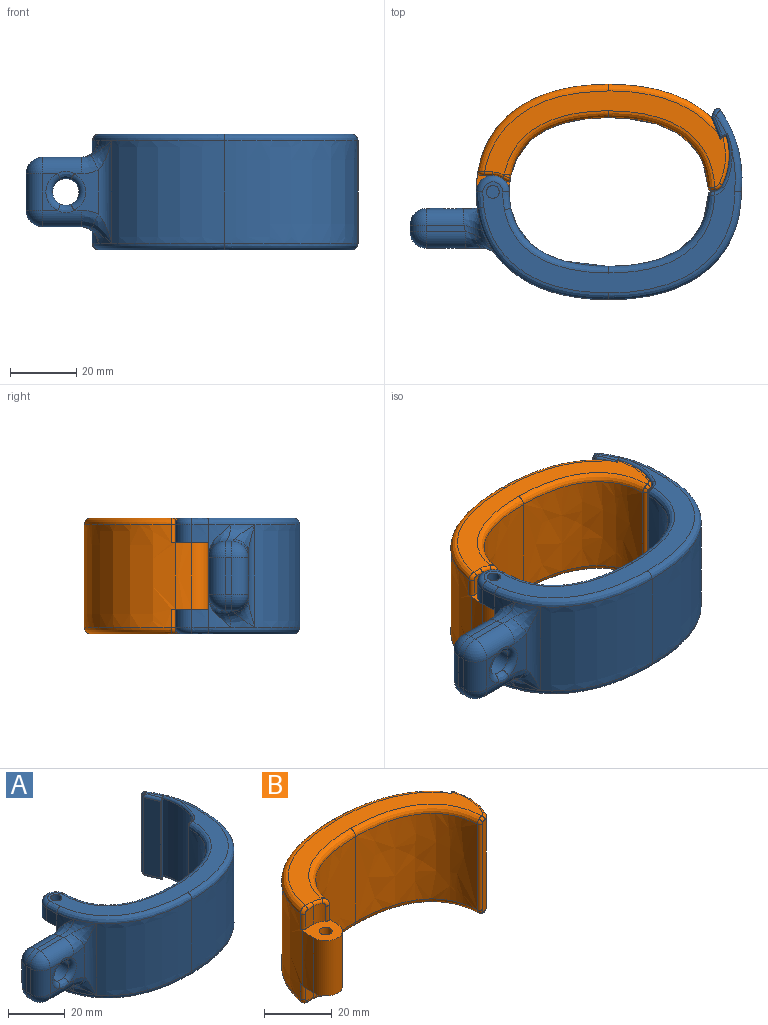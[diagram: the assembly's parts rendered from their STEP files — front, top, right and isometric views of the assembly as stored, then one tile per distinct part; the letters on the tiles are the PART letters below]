
ASSEMBLY  parts=2 mates=1
PART A: 105 faces, bbox 103.2x59x35.3 mm
  f0: cylinder r=1.95mm len=5.5mm, axis (0,0,-1), area 67.4mm2, adj f28,f97
  f1: plane 6.24x3.35mm, normal (0,0,-1), area 6.3mm2, adj f69,f72,f73,f99
  f2: plane 6.24x3.35mm, normal (0,0,1), area 6.3mm2, adj f61,f76,f78,f103
  f3: plane 20x10.6mm, normal (0,1,0), area 132.4mm2, adj f5,f7,f27,f28,f29,f38,f40,f43
  f4: plane 13.52x7.52mm, normal (0,-1,0), area 58.4mm2, adj f36,f41,f44,f54,f55,f81
  f5: extruded ~9.18x6.72mm, area 32mm2, adj f3,f9,f38,f70
  f6: extruded ~34.09x31mm, area 1178.9mm2, adj f13,f36,f62,f70
  f7: extruded ~9.18x6.72mm, area 32mm2, adj f3,f12,f43,f62
  f8: cylinder r=5mm len=10mm, axis (0,0,-1), area 86.4mm2, adj f9,f10,f28,f67
  f9: extruded ~5.5x5mm, area 27.6mm2, adj f5,f8,f28,f68
  f10: extruded ~31x5mm, area 118.7mm2, adj f8,f11,f22,f28,f29,f58,f66,f87
  f11: cylinder r=5mm len=10mm, axis (0,0,-1), area 86.4mm2, adj f10,f12,f29,f59
  f12: extruded ~5.5x5mm, area 27.6mm2, adj f7,f11,f29,f60
  f13: extruded ~40x32.5mm, area 1806.6mm2, adj f6,f14,f63,f71
  f14: cylinder r=36mm len=31mm, axis (0,0,-1), area 809.5mm2, adj f13,f61,f69,f75
  f15: extruded ~33x2.05mm, area 73.3mm2, adj f16,f73,f74,f75,f77,f78
  f16: plane 33x6.17mm, normal (-0.93,-0.37,0), area 219.4mm2, adj f15,f72,f76,f101
  f17: plane 34.65x1.88mm, normal (0.54,-0.84,0), area 60.8mm2, adj f18,f88,f96,f98,f99,f100,f101,f102
  f18: cylinder r=20mm len=33mm, axis (0,0,-1), area 529.8mm2, adj f17,f19,f88,f96
  f19: cylinder r=3mm len=33mm, axis (0,0,-1), area 107.5mm2, adj f18,f20,f89,f90,f94,f95
  f20: plane 32.43x0.3mm, normal (0,1,0), area 9.6mm2, adj f19,f91,f92,f93
  f21: extruded ~31x29.98mm, area 1289.7mm2, adj f22,f56,f64,f92
  f22: extruded ~31x29.55mm, area 1163.8mm2, adj f10,f21,f57,f65
  f23: cylinder r=1.95mm len=7.5mm, axis (0,0,-1), area 91.9mm2, adj f24,f29
  f24: plane 76.22x42.84mm, normal (0,0,1), area 626.1mm2, adj f23,f56,f57,f58,f59,f60,f61,f62
  f25: plane 76.22x42.84mm, normal (0,0,-1), area 638mm2, adj f64,f65,f66,f67,f68,f69,f70,f71
  f26: plane 11x4.6mm, normal (0,1,0), area 22.1mm2, adj f40,f46,f47,f85
  f27: cylinder r=5mm len=20mm, axis (0,0,1), area 131.1mm2, adj f3,f28,f29,f87
  f28: plane 10.08x10.03mm, normal (0,0,1), area 71.5mm2, adj f0,f3,f8,f9,f10,f27,f87
  f29: plane 10.08x10.03mm, normal (0,0,-1), area 71.5mm2, adj f3,f10,f11,f12,f23,f27,f87
  f30: plane 11.78x2mm, normal (0,0,1), area 23mm2, adj f35,f47,f51,f55
  f31: plane 11x4.6mm, normal (0,-1,0), area 22.1mm2, adj f44,f50,f55,f80
  f32: plane 11.78x2mm, normal (0,0,-1), area 23mm2, adj f37,f40,f44,f45
  f33: plane 11x2mm, normal (-1,0,0), area 22mm2, adj f45,f46,f50,f51
  f34: cylinder r=4mm len=8mm, axis (0,1,0), area 201.1mm2, adj f79,f80,f81,f82,f83,f84,f85,f86
  f35: bspline ~16.06x11.16mm, area 34.4mm2, adj f30,f43,f52,f54,f62
  f36: cylinder r=5mm len=31mm, axis (0,0,-1), area 103mm2, adj f4,f6,f39,f52
  f37: bspline ~16.06x11.16mm, area 34.4mm2, adj f32,f38,f39,f41,f70
  f38: bspline ~12.05x11.84mm, area 54.9mm2, adj f3,f5,f37,f40
  f39: bspline ~9.43x7.13mm, area 19.5mm2, adj f36,f37,f41
  f40: cylinder r=5mm len=11.21mm, axis (1,0,0), area 85.3mm2, adj f3,f26,f32,f38,f42,f86
  f41: bspline ~6.48x5.93mm, area 28.7mm2, adj f4,f37,f39,f44
  f42: sphere r=5mm, area 53.5mm2, adj f40,f45,f46
  f43: bspline ~12.05x11.84mm, area 54.9mm2, adj f3,f7,f35,f47
  f44: cylinder r=5mm len=11.78mm, axis (-1,0,0), area 89.8mm2, adj f4,f31,f32,f41,f48,f79
  f45: cylinder r=5mm len=5mm, axis (0,-1,0), area 15.7mm2, adj f32,f33,f42,f48
  f46: cylinder r=5mm len=11mm, axis (0,0,-1), area 86.4mm2, adj f26,f33,f42,f49
  f47: cylinder r=5mm len=11.21mm, axis (-1,0,0), area 85.3mm2, adj f3,f26,f30,f43,f49,f83
  f48: sphere r=5mm, area 39.3mm2, adj f44,f45,f50
  f49: sphere r=5mm, area 53.5mm2, adj f46,f47,f51
  f50: cylinder r=5mm len=11mm, axis (0,0,1), area 86.4mm2, adj f31,f33,f48,f53
  f51: cylinder r=5mm len=5mm, axis (0,1,0), area 15.7mm2, adj f30,f33,f49,f53
  f52: bspline ~9.43x7.13mm, area 19.5mm2, adj f35,f36,f54
  f53: sphere r=5mm, area 39.3mm2, adj f50,f51,f55
  f54: bspline ~7.39x5.93mm, area 28.7mm2, adj f4,f35,f52,f55
  f55: cylinder r=5mm len=11.78mm, axis (1,0,0), area 89.8mm2, adj f4,f30,f31,f53,f54,f82
  f56: bspline ~45.49x24.18mm, area 134.3mm2, adj f21,f24,f57,f93,f94
  f57: bspline ~40.59x27mm, area 121.1mm2, adj f22,f24,f56,f58
  f58: bspline ~6.58x2.5mm, area 16.2mm2, adj f10,f24,f57,f59
  f59: torus R=3mm, axis (0,0,1), area 42.2mm2, adj f11,f24,f58,f60
  f60: bspline ~6.12x2.43mm, area 15.4mm2, adj f12,f24,f59,f62
  f61: torus R=34mm, axis (0,0,1), area 78.4mm2, adj f2,f14,f24,f63,f77,f96,f104
  f62: bspline ~50.61x44.89mm, area 164mm2, adj f6,f7,f24,f35,f60,f63
  f63: bspline ~57.27x33.99mm, area 179.7mm2, adj f13,f24,f61,f62
  f64: bspline ~45.49x24.18mm, area 134.3mm2, adj f21,f25,f65,f90,f91
  f65: bspline ~40.59x27mm, area 121.1mm2, adj f22,f25,f64,f66
  f66: bspline ~7.29x2.64mm, area 16.2mm2, adj f10,f25,f65,f67
  f67: torus R=3mm, axis (0,0,1), area 42.2mm2, adj f8,f25,f66,f68
  f68: bspline ~6.12x2.43mm, area 15.4mm2, adj f9,f25,f67,f70
  f69: torus R=34mm, axis (0,0,1), area 78.4mm2, adj f1,f14,f25,f71,f74,f88,f98
  f70: bspline ~50.61x44.89mm, area 164.1mm2, adj f5,f6,f25,f37,f68,f71
  f71: bspline ~57.27x33.99mm, area 179.7mm2, adj f13,f25,f69,f70
  f72: cylinder r=1mm len=6.54mm, axis (0.37,-0.93,0), area 10mm2, adj f1,f16,f73,f100
  f73: bspline ~2.29x1.78mm, area 1.4mm2, adj f1,f15,f72,f74
  f74: bspline ~3.64x2.42mm, area 5.4mm2, adj f15,f69,f73,f75
  f75: cylinder r=1mm len=31mm, axis (0,0,-1), area 66.5mm2, adj f14,f15,f74,f77
  f76: cylinder r=1mm len=6.54mm, axis (-0.37,0.93,0), area 10mm2, adj f2,f16,f78,f102
  f77: bspline ~3.64x2.42mm, area 5.4mm2, adj f15,f61,f75,f78
  f78: bspline ~2.29x1.78mm, area 1.4mm2, adj f2,f15,f76,f77
  f79: bspline ~6.58x3.08mm, area 13.3mm2, adj f34,f44,f80,f81
  f80: torus R=6mm, axis (0,-1,0), area 34.4mm2, adj f31,f34,f79,f82
  f81: torus R=6mm, axis (0,-1,0), area 34.4mm2, adj f4,f34,f79,f82
  f82: bspline ~6.58x3.08mm, area 13.3mm2, adj f34,f55,f80,f81
  f83: bspline ~6.58x3.08mm, area 13.3mm2, adj f34,f47,f84,f85
  f84: torus R=6mm, axis (0,-1,0), area 34.4mm2, adj f3,f34,f83,f86
  f85: torus R=6mm, axis (0,-1,0), area 34.4mm2, adj f26,f34,f83,f86
  f86: bspline ~6.58x3.08mm, area 13.3mm2, adj f34,f40,f84,f85
  f87: cylinder r=1mm len=20mm, axis (0,0,-1), area 12.5mm2, adj f10,f27,f28,f29
  f88: torus R=21mm, axis (0,0,1), area 25.1mm2, adj f17,f18,f25,f69,f89,f98
  f89: torus R=4mm, axis (0,0,1), area 4.8mm2, adj f19,f25,f88,f90
  f90: bspline ~2.14x1.48mm, area 1.8mm2, adj f19,f64,f89,f91
  f91: bspline ~2.15x1.48mm, area 2mm2, adj f20,f64,f90,f92
  f92: cylinder r=1mm len=31mm, axis (0,0,-1), area 47.7mm2, adj f20,f21,f91,f93
  f93: bspline ~2.15x1.48mm, area 2mm2, adj f20,f56,f92,f94
  f94: bspline ~2.14x1.48mm, area 1.8mm2, adj f19,f56,f93,f95
  f95: torus R=4mm, axis (0,0,1), area 4.8mm2, adj f19,f24,f94,f96
  f96: torus R=21mm, axis (0,0,1), area 25.1mm2, adj f17,f18,f24,f61,f95,f104
  f97: plane 3.9x3.9mm, normal (0,0,1), area 11.9mm2, adj f0
  f98: bspline ~0.92x0.68mm, area 0.1mm2, adj f17,f69,f88,f99
  f99: cylinder r=0.2mm len=1.2mm, axis (0.84,0.54,0), area 0.4mm2, adj f1,f17,f98,f100
  f100: bspline ~1.13x1mm, area 0.5mm2, adj f17,f72,f99,f101
  f101: cylinder r=0.2mm len=33mm, axis (0,0,-1), area 11.6mm2, adj f16,f17,f100,f102
  f102: bspline ~1.13x1.05mm, area 0.5mm2, adj f17,f76,f101,f103
  f103: cylinder r=0.2mm len=1.2mm, axis (-0.84,-0.54,0), area 0.4mm2, adj f2,f17,f102,f104
  f104: bspline ~0.92x0.68mm, area 0.1mm2, adj f17,f61,f96,f103
PART B: 57 faces, bbox 93.2x38.6x36.3 mm
  f0: extruded ~20x5mm, area 100.3mm2, adj f1,f12,f16,f19
  f1: cylinder r=5mm len=20mm, axis (0,0,-1), area 314.2mm2, adj f0,f3,f16,f19
  f2: cylinder r=1.95mm len=20mm, axis (0,0,-1), area 245mm2, adj f16,f19
  f3: extruded ~31x5mm, area 111.3mm2, adj f1,f4,f16,f19,f25,f30,f36,f42
  f4: extruded ~31x29.55mm, area 1163.8mm2, adj f3,f5,f24,f29
  f5: extruded ~31x29.97mm, area 1274.7mm2, adj f4,f23,f28,f47
  f6: plane 32.47x0.32mm, normal (0,-1,0), area 10.3mm2, adj f7,f46,f47,f48
  f7: cylinder r=3mm len=33mm, axis (0,0,-1), area 118.9mm2, adj f6,f8,f44,f45,f46,f48,f49,f50
  f8: cylinder r=20mm len=33mm, axis (0,0,-1), area 499.9mm2, adj f7,f43,f51,f54
  f9: plane 34.6x1.47mm, normal (-0.54,0.84,0), area 60mm2, adj f10,f52,f53,f54,f55,f56
  f10: plane 36.13x7.71mm, normal (0.93,0.37,0), area 237mm2, adj f9,f11,f13,f14,f22,f27,f52,f56
  f11: extruded ~31x30.96mm, area 1033.2mm2, adj f10,f12,f22,f27
  f12: extruded ~39.68x31mm, area 1638.2mm2, adj f0,f11,f16,f19,f21,f26,f31,f37
  f13: plane 72.75x28.98mm, normal (0,0,1), area 534.1mm2, adj f10,f26,f27,f28,f29,f30,f33,f34
  f14: plane 72.74x28.98mm, normal (0,0,-1), area 534.1mm2, adj f10,f21,f22,f23,f24,f25,f39,f40
  f15: plane 6.5x3.51mm, normal (0,-1,0), area 22.6mm2, adj f16,f17,f31,f32,f33
  f16: plane 11.28x10.4mm, normal (0,0,1), area 73.3mm2, adj f0,f1,f2,f3,f12,f15,f17,f31
  f17: cylinder r=5mm len=6.5mm, axis (0,0,-1), area 25.5mm2, adj f15,f16,f34,f35,f36
  f18: cylinder r=5mm len=6.5mm, axis (0,0,1), area 25.5mm2, adj f19,f20,f40,f41,f42
  f19: plane 11.27x10.4mm, normal (0,0,-1), area 73.3mm2, adj f0,f1,f2,f3,f12,f18,f20,f37
  f20: plane 6.5x3.51mm, normal (0,-1,0), area 22.6mm2, adj f18,f19,f37,f38,f39
  f21: bspline ~48.22x27.16mm, area 160.1mm2, adj f12,f14,f22,f38
  f22: bspline ~61.17x31.46mm, area 109.9mm2, adj f10,f11,f14,f21
  f23: bspline ~45.64x24.39mm, area 132.7mm2, adj f5,f14,f24,f45,f46
  f24: bspline ~40.59x27mm, area 121.1mm2, adj f4,f14,f23,f25
  f25: bspline ~2.86x2.41mm, area 2.2mm2, adj f3,f14,f24,f41
  f26: bspline ~48.22x27.16mm, area 160.1mm2, adj f12,f13,f27,f32
  f27: bspline ~61.17x31.46mm, area 109.9mm2, adj f10,f11,f13,f26
  f28: bspline ~45.64x24.39mm, area 132.7mm2, adj f5,f13,f29,f48,f49
  f29: bspline ~40.59x27mm, area 121.1mm2, adj f4,f13,f28,f30
  f30: bspline ~2.86x2.41mm, area 2.2mm2, adj f3,f13,f29,f35
  f31: cylinder r=1mm len=5.5mm, axis (0,0,-1), area 9.6mm2, adj f12,f15,f16,f32
  f32: bspline ~2.65x2.49mm, area 4.4mm2, adj f15,f26,f31,f33
  f33: cylinder r=1mm len=2.5mm, axis (-1,0,0), area 3.9mm2, adj f13,f15,f32,f34
  f34: torus R=6mm, axis (0,0,1), area 5.1mm2, adj f13,f17,f33,f35
  f35: bspline ~3.04x2.72mm, area 5.3mm2, adj f17,f30,f34,f36
  f36: cylinder r=1mm len=5.5mm, axis (0,0,-1), area 12.2mm2, adj f3,f16,f17,f35
  f37: cylinder r=1mm len=5.5mm, axis (0,0,-1), area 9.6mm2, adj f12,f19,f20,f38
  f38: bspline ~2.65x2.49mm, area 4.4mm2, adj f20,f21,f37,f39
  f39: cylinder r=1mm len=2.5mm, axis (1,0,0), area 3.9mm2, adj f14,f20,f38,f40
  f40: torus R=6mm, axis (0,0,1), area 5.1mm2, adj f14,f18,f39,f41
  f41: bspline ~3.04x2.72mm, area 5.3mm2, adj f18,f25,f40,f42
  f42: cylinder r=1mm len=5.5mm, axis (0,0,-1), area 12.2mm2, adj f3,f18,f19,f41
  f43: torus R=19mm, axis (0,0,1), area 23.2mm2, adj f8,f14,f44,f53
  f44: torus R=2mm, axis (0,0,1), area 3.7mm2, adj f7,f14,f43,f45
  f45: bspline ~1.99x1.33mm, area 2mm2, adj f7,f23,f44,f46
  f46: bspline ~1.97x1.47mm, area 2.2mm2, adj f6,f7,f23,f45,f47
  f47: cylinder r=1mm len=31mm, axis (0,0,-1), area 47.2mm2, adj f5,f6,f46,f48
  f48: bspline ~1.97x1.47mm, area 2.2mm2, adj f6,f7,f28,f47,f49
  f49: bspline ~1.94x1.29mm, area 2mm2, adj f7,f28,f48,f50
  f50: torus R=2mm, axis (0,0,1), area 3.7mm2, adj f7,f13,f49,f51
  f51: torus R=19mm, axis (0,0,1), area 23.2mm2, adj f8,f13,f50,f55
  f52: cylinder r=0.2mm len=0.91mm, axis (-0.84,-0.54,0), area 0.3mm2, adj f9,f10,f14,f53
  f53: bspline ~1.24x1.19mm, area 0.5mm2, adj f9,f43,f52,f54
  f54: cylinder r=0.2mm len=33mm, axis (0,0,-1), area 12.1mm2, adj f8,f9,f53,f55
  f55: bspline ~1.23x1.05mm, area 0.5mm2, adj f9,f51,f54,f56
  f56: cylinder r=0.2mm len=0.91mm, axis (0.84,0.54,0), area 0.3mm2, adj f9,f10,f13,f55
PLACE A t=(0.2,3.77,2.57)mm fixed
PLACE B rot(axis=(0,0,-1),0.1deg) t=(0.2,3.74,2.57)mm
MATE revolute B.f2 <-> A.f0  axis (0,0,1) through (-34.8,3.77,12.57)mm
